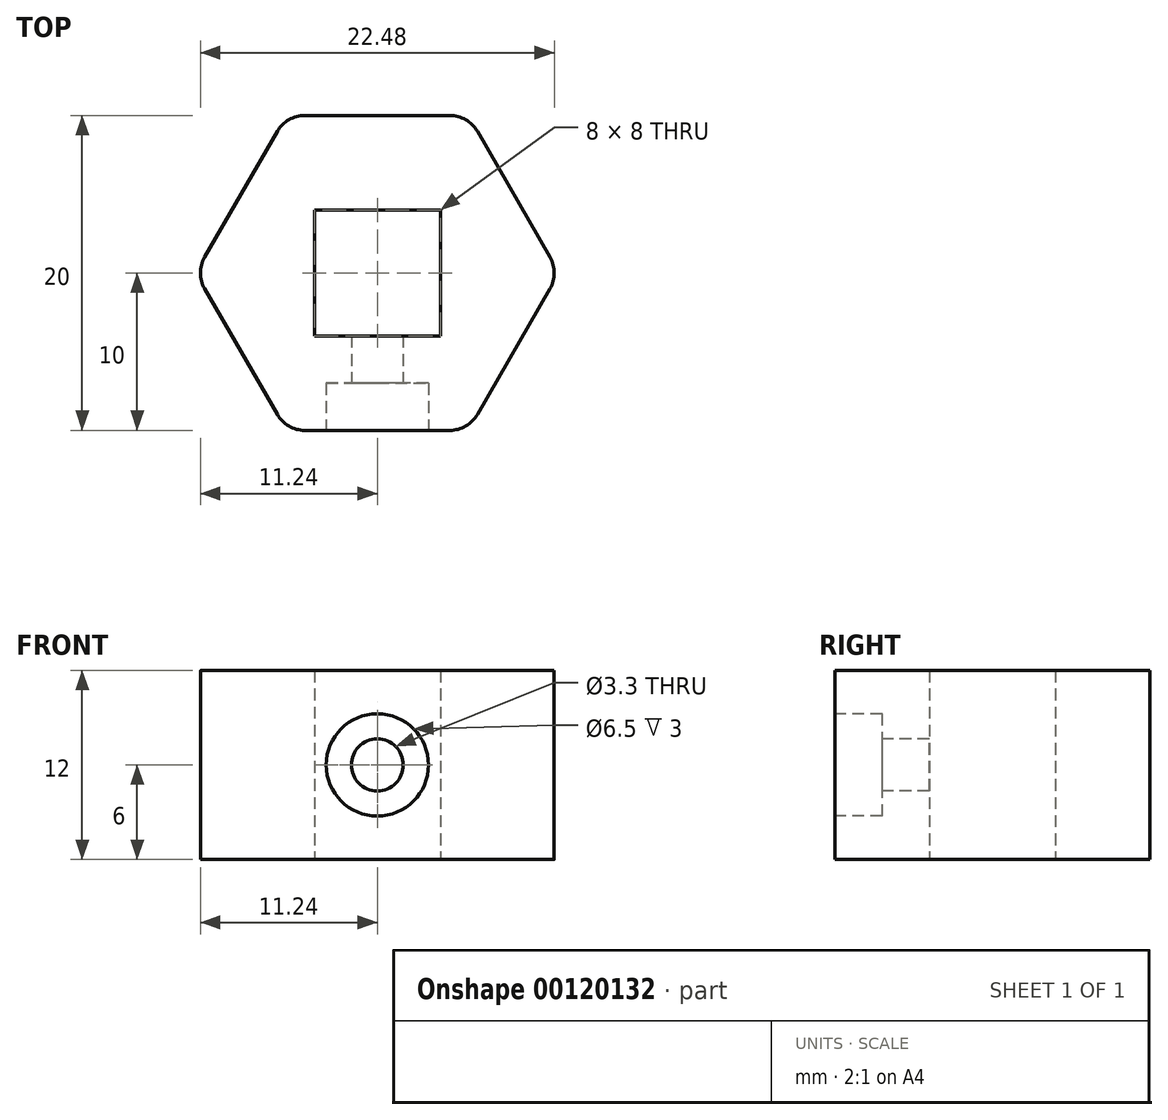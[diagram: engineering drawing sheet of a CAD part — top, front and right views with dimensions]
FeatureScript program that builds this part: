
annotation { "Feature Type Name" : "Feature", "Feature Type Description" : "" }
export const myFeature = defineFeature(function(context is Context, id is Id, definition is map)
    precondition{}
    {
        {
            var Q0;
            Q0=qCreatedBy(makeId("Top.planeOp"),FACE);
            var sketch = newSketch(context, id + "F0", { "sketchPlane" : qUnion([Q0])});
            skCircle(sketch, "E0", {"center": v(0, 0) * mm, "radius": 37 * mm, "construction": true});
            skLineSegment(sketch, "E1.bottom", {"start": v(4, -4) * mm, "end": v(-4, -4) * mm});
            skLineSegment(sketch, "E1.top", {"start": v(4, 4) * mm, "end": v(-4, 4) * mm});
            skLineSegment(sketch, "E1.left", {"start": v(4, -4) * mm, "end": v(4, 4) * mm});
            skLineSegment(sketch, "E1.right", {"start": v(-4, -4) * mm, "end": v(-4, 4) * mm});
            skCircle(sketch, "E2.cCircle", {"center": v(0, 0) * mm, "radius": 10 * mm, "construction": true});
            skLineSegment(sketch, "E2.0", {"start": v(11.55, 0) * mm, "end": v(5.77, -10) * mm});
            skLineSegment(sketch, "E2.1", {"start": v(5.77, -10) * mm, "end": v(-5.77, -10) * mm});
            skLineSegment(sketch, "E2.2", {"start": v(-5.77, -10) * mm, "end": v(-11.55, 0) * mm});
            skLineSegment(sketch, "E2.3", {"start": v(-11.55, 0) * mm, "end": v(-5.77, 10) * mm});
            skLineSegment(sketch, "E2.4", {"start": v(-5.77, 10) * mm, "end": v(5.77, 10) * mm});
            skLineSegment(sketch, "E2.5", {"start": v(5.77, 10) * mm, "end": v(11.55, 0) * mm});
            skPoint(sketch, "E2.0.midPoint", {"position": v(8.66, -5) * mm});
            skSolve(sketch);
        }
        {
            var Q0;
            Q0=makeQuery(id+"F0.imprint","IMPRINT",FACE,{"disambiguationData":[TD([[makeQuery(id+"F0.imprint","IMPRINT",EDGE,{"derivedFrom":sQuery(id+"F0.wireOp",EDGE,"E1.bottom")}),1.0]])]});
            extrude(context, id + "F1", {"entities" : qUnion([Q0]), "depth" : 12 * mm});
        }
        {
            var Q0;
            Q0=makeQuery(id+"F1.opExtrude","SWEPT_FACE",FACE,{"disambiguationData":[OSD([sQuery(id+"F0.wireOp",EDGE,"E2.1")])]});
            var sketch = newSketch(context, id + "F2", { "sketchPlane" : qUnion([Q0])});
            skLineSegment(sketch, "E3", {"start": v(-5.77, 12) * mm, "end": v(5.77, 0) * mm, "construction": true});
            skPoint(sketch, "E4", {"position": v(0, 6) * mm});
            skSolve(sketch);
        }
        {
            var Q0;
            Q0=sQuery(id+"F2.wireOp",VERTEX,"E4");
            var Q1;
            Q1=makeQuery(id+"F1.opExtrude","SWEPT_BODY",BODY,{"disambiguationData":[OSD([sQuery(id+"F0.wireOp",EDGE,"E1.bottom"),sQuery(id+"F0.wireOp",EDGE,"E1.top"),sQuery(id+"F0.wireOp",EDGE,"E1.left"),sQuery(id+"F0.wireOp",EDGE,"E1.right"),sQuery(id+"F0.wireOp",EDGE,"E2.0"),sQuery(id+"F0.wireOp",EDGE,"E2.1"),sQuery(id+"F0.wireOp",EDGE,"E2.2"),sQuery(id+"F0.wireOp",EDGE,"E2.3"),sQuery(id+"F0.wireOp",EDGE,"E2.4"),sQuery(id+"F0.wireOp",EDGE,"E2.5")])]});
            hole(context, id + "F3", {"style" : HoleStyle.C_BORE, "endStyle" : HoleEndStyle.BLIND, "standardTappedOrClearance" : lookupTablePath({ "standard" : "ISO", "fit" : "Normal", "size" : "M3", "type" : "Clearance" }), "standardBlindInLast" : lookupTablePath({ "fit" : "Standard", "standard" : "ISO", "size" : "M3", "type" : "Clearance" }), "holeDiameter" : 3.3 * mm, "cBoreDiameter" : 6.5 * mm, "cBoreDepth" : 3 * mm, "holeDepth" : 12 * mm, "locations" : qUnion([Q0]), "scope" : qUnion([Q1])});
        }
        {
            var Q0;
            Q0=makeQuery(id+"F1.opExtrude","SWEPT_EDGE",EDGE,{"disambiguationData":[OSD([sQuery(id+"F0.wireOp",EDGE,"E2.2"),sQuery(id+"F0.wireOp",EDGE,"E2.3")])]});
            var Q1;
            Q1=makeQuery(id+"F1.opExtrude","SWEPT_EDGE",EDGE,{"disambiguationData":[OSD([sQuery(id+"F0.wireOp",EDGE,"E2.1"),sQuery(id+"F0.wireOp",EDGE,"E2.2")])]});
            var Q2;
            Q2=makeQuery(id+"F1.opExtrude","SWEPT_EDGE",EDGE,{"disambiguationData":[OSD([sQuery(id+"F0.wireOp",EDGE,"E2.0"),sQuery(id+"F0.wireOp",EDGE,"E2.1")])]});
            var Q3;
            Q3=makeQuery(id+"F1.opExtrude","SWEPT_EDGE",EDGE,{"disambiguationData":[OSD([sQuery(id+"F0.wireOp",EDGE,"E2.0"),sQuery(id+"F0.wireOp",EDGE,"E2.5")])]});
            var Q4;
            Q4=makeQuery(id+"F1.opExtrude","SWEPT_EDGE",EDGE,{"disambiguationData":[OSD([sQuery(id+"F0.wireOp",EDGE,"E2.4"),sQuery(id+"F0.wireOp",EDGE,"E2.5")])]});
            var Q5;
            Q5=makeQuery(id+"F1.opExtrude","SWEPT_EDGE",EDGE,{"disambiguationData":[OSD([sQuery(id+"F0.wireOp",EDGE,"E2.3"),sQuery(id+"F0.wireOp",EDGE,"E2.4")])]});
            fillet(context, id + "F4", {"entities" : qUnion([Q0, Q1, Q2, Q3, Q4, Q5]), "radius" : 2 * mm, "tangentPropagation" : true, "allowEdgeOverflow" : false});
        }
    });
